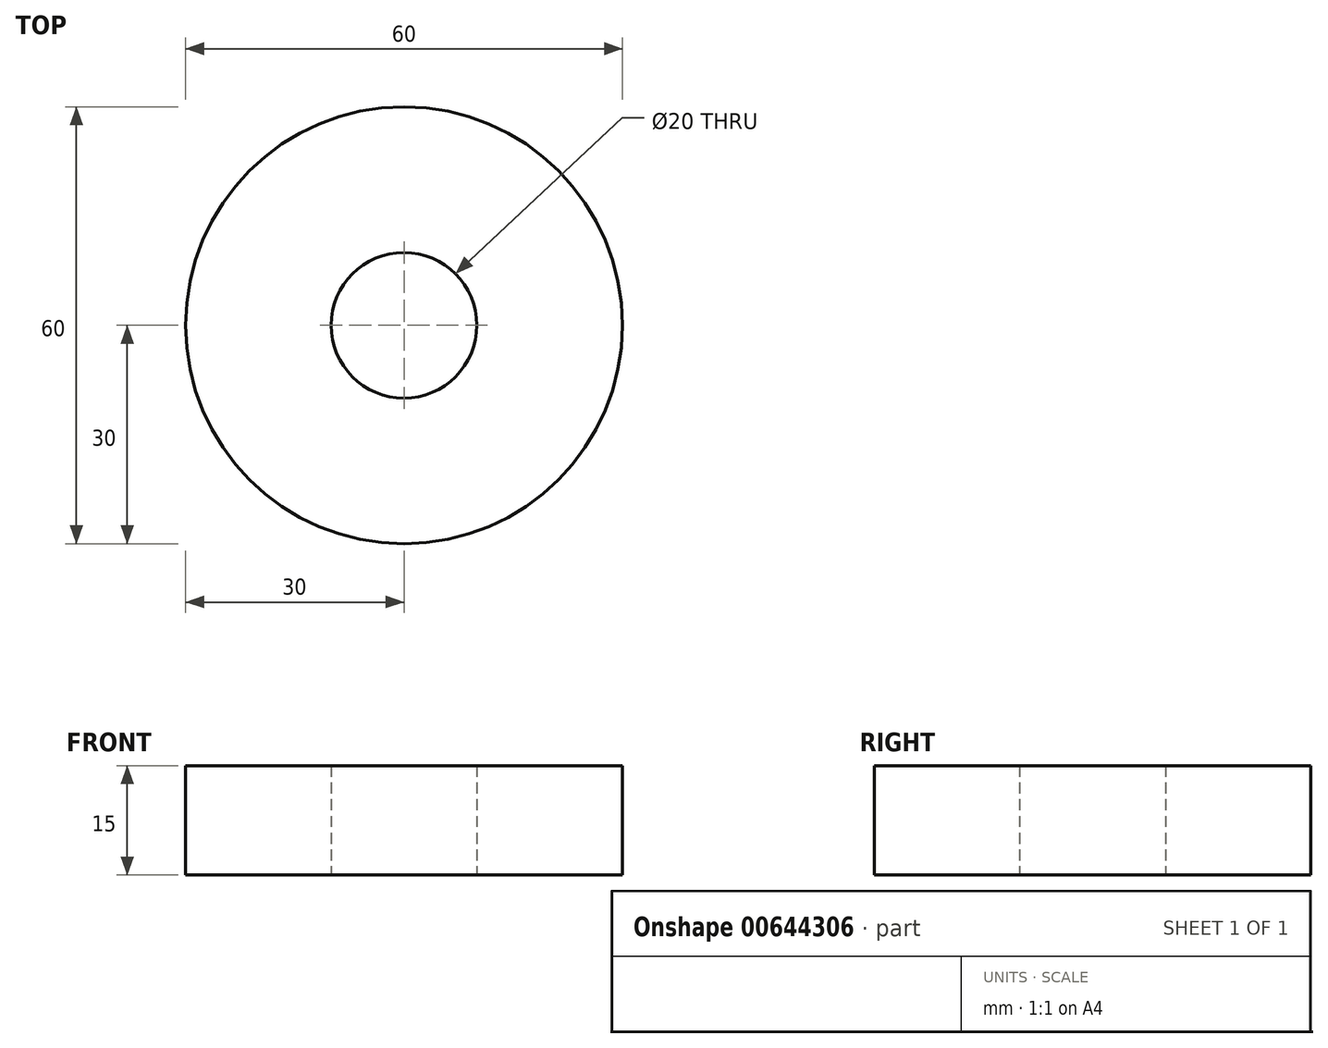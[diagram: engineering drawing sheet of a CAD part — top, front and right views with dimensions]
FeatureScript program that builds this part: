
annotation { "Feature Type Name" : "Feature", "Feature Type Description" : "" }
export const myFeature = defineFeature(function(context is Context, id is Id, definition is map)
    precondition{}
    {
        {
            var Q0;
            Q0=qCreatedBy(makeId("Top.planeOp"),FACE);
            var sketch = newSketch(context, id + "F0", { "sketchPlane" : qUnion([Q0])});
            skCircle(sketch, "E0", {"center": v(0, 0) * mm, "radius": 10 * mm});
            skCircle(sketch, "E1.0", {"center": v(0, 0) * mm, "radius": 30 * mm});
            skSolve(sketch);
        }
        {
            var Q0;
            Q0 = qSketchRegion(id + "F0", true);
            extrude(context, id + "F1", {"entities" : qUnion([Q0]), "depth" : 15 * mm, "offsetDistance" : 25 * mm});
        }
    });
